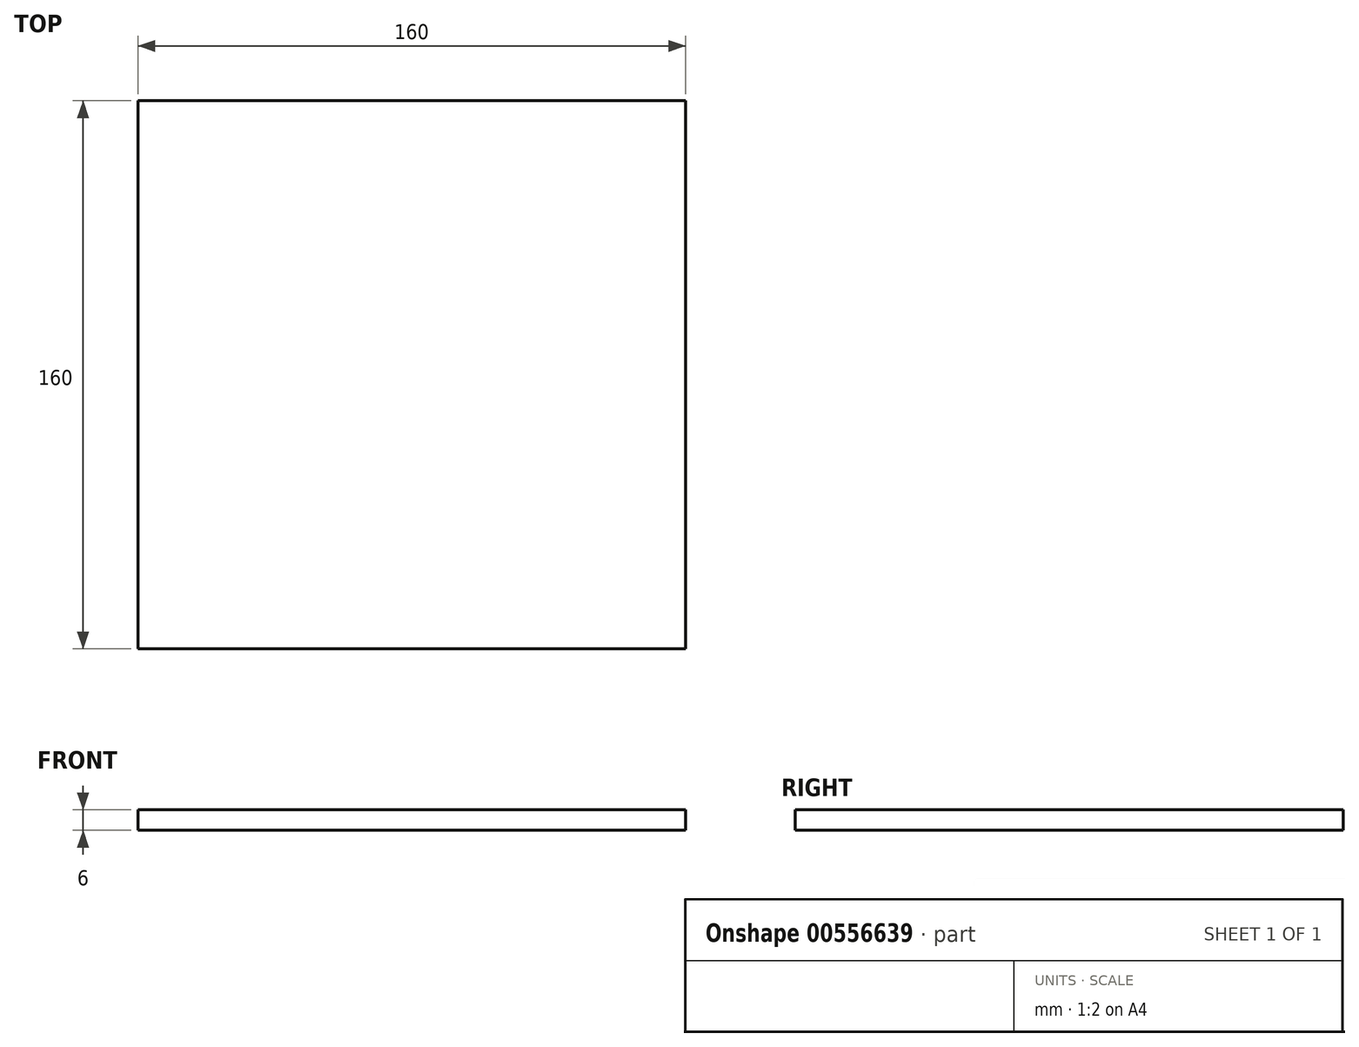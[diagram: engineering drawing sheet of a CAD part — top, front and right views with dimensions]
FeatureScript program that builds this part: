
annotation { "Feature Type Name" : "Feature", "Feature Type Description" : "" }
export const myFeature = defineFeature(function(context is Context, id is Id, definition is map)
    precondition{}
    {
        {
            var Q0;
            Q0=qCreatedBy(makeId("Top.planeOp"),FACE);
            var sketch = newSketch(context, id + "F0", { "sketchPlane" : qUnion([Q0])});
            skLineSegment(sketch, "E0", {"start": v(0, 0) * mm, "end": v(0, -160) * mm});
            skLineSegment(sketch, "E1", {"start": v(0, -160) * mm, "end": v(160, -160) * mm});
            skLineSegment(sketch, "E2", {"start": v(160, -160) * mm, "end": v(160, 0) * mm});
            skLineSegment(sketch, "E3", {"start": v(160, 0) * mm, "end": v(0, 0) * mm});
            skSolve(sketch);
        }
        {
            var Q0;
            Q0=makeQuery(id+"F0.imprint","IMPRINT",FACE,{"disambiguationData":[TD([[makeQuery(id+"F0.imprint","IMPRINT",EDGE,{"derivedFrom":sQuery(id+"F0.wireOp",EDGE,"E0")}),1.0]])]});
            extrude(context, id + "F1", {"entities" : qUnion([Q0]), "depth" : 6 * mm, "offsetDistance" : 25 * mm});
        }
    });
